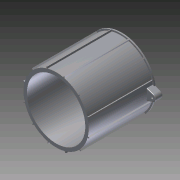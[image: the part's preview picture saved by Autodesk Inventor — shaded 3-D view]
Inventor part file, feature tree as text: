
AUTODESK INVENTOR PART (.ipt)
format: ipt  version: 2011 (Build 150239000, 239)  size: 710,656 bytes
history: native  units: in
note: dims shown in document units (in); Inventor stores cm internally (conversion verified against a paired STEP export)
features: extrude x11, sketch x11, pattern_circular x4, fillet x1, projected_geometry x1
ambient origin geometry x8: Origin, YZ Plane, XZ Plane, XY Plane, X Axis, Y Axis, Z Axis, Center Point
bodies: Solid1 (feature_tree)
feature tree (28):
  extrude  "Extrusion1"  Depth=3.15in
  extrude  "Extrusion2"  Depth=3.0in
  extrude  "Extrusion3"  Depth=3.375in TaperAngle=0.0deg
  extrude  "Extrusion4"  Depth=1.15in
  extrude  "Extrusion5"  Depth=0.05in
  pattern_circular  "Circular Pattern1"  Count=12 Angle=360.0deg
  extrude  "Extrusion6"  Depth=4.7244in TaperAngle=360.0deg
  pattern_circular  "Circular Pattern2"  [2 undecoded]
  extrude  "Extrusion7"  Depth=0.45in TaperAngle=0.0deg
  pattern_circular  "Circular Pattern3"  Count=12 Angle=360.0deg
  extrude  "Extrusion8"  Depth=0.075in
  pattern_circular  "Circular Pattern4"  [2 undecoded]
  extrude  "Extrusion9"  Depth=0.15in TaperAngle=0.0deg
  extrude  "Extrusion10"  Depth=4.7244in TaperAngle=360.0deg
  extrude  "Extrusion11"  Depth=3.7in TaperAngle=0.0deg
  fillet  "Fillet1"  Radius=4.7244in
  sketch  "Sketch1"  dims[d0=3.35in d1=3.15in]
  sketch  "Sketch2"  dims[d2=3.375in d3=0.0in d4=3.0in]
  sketch  "Sketch3"  dims[d5=0.125in d6=0.0in d7=3.375in d8=0.0in]
  sketch  "Sketch4"  dims[d9=0.45in d10=0.0in d11=1.15in]
  sketch  "Sketch5"  dims[d13=0.05in d15=0.05in]
  sketch  "Sketch6"  dims[d16=0.05in d18=4.7244in d20=360.0deg]
  sketch  "Sketch7"  dims[d22=0.075in d23=0.0in d24=4.7244in d25=360.0deg]
  projected_geometry  "Projected Loop1"
  sketch  "Sketch8"  dims[d27=0.1168in]
  sketch  "Sketch9"  dims[d28=0.675in]
  sketch  "Sketch10"  dims[d29=0.2in]
  sketch  "Sketch12"  dims[d30=0.25in d31=0.075in d32=0.45in d33=0.0in d34=4.7244in d35=360.0deg d38=0.075in d39=0.075in d40=0.15in d41=0.0in d42=4.7244in d43=360.0deg d45=3.7in d46=0.0in d47=4.7244in d48=360.0deg d50=0.07in d51=0.0in d52=1.0in d53=0.0in d60=0.375in d61=0.125in d63=0.375in d64=0.0in d65=0.0312in]
note: 4 required parameter values undecoded (feature->parameter linkage not recoverable at this tier; creation-order binding heuristic only, values carry confidence <= 0.55)
